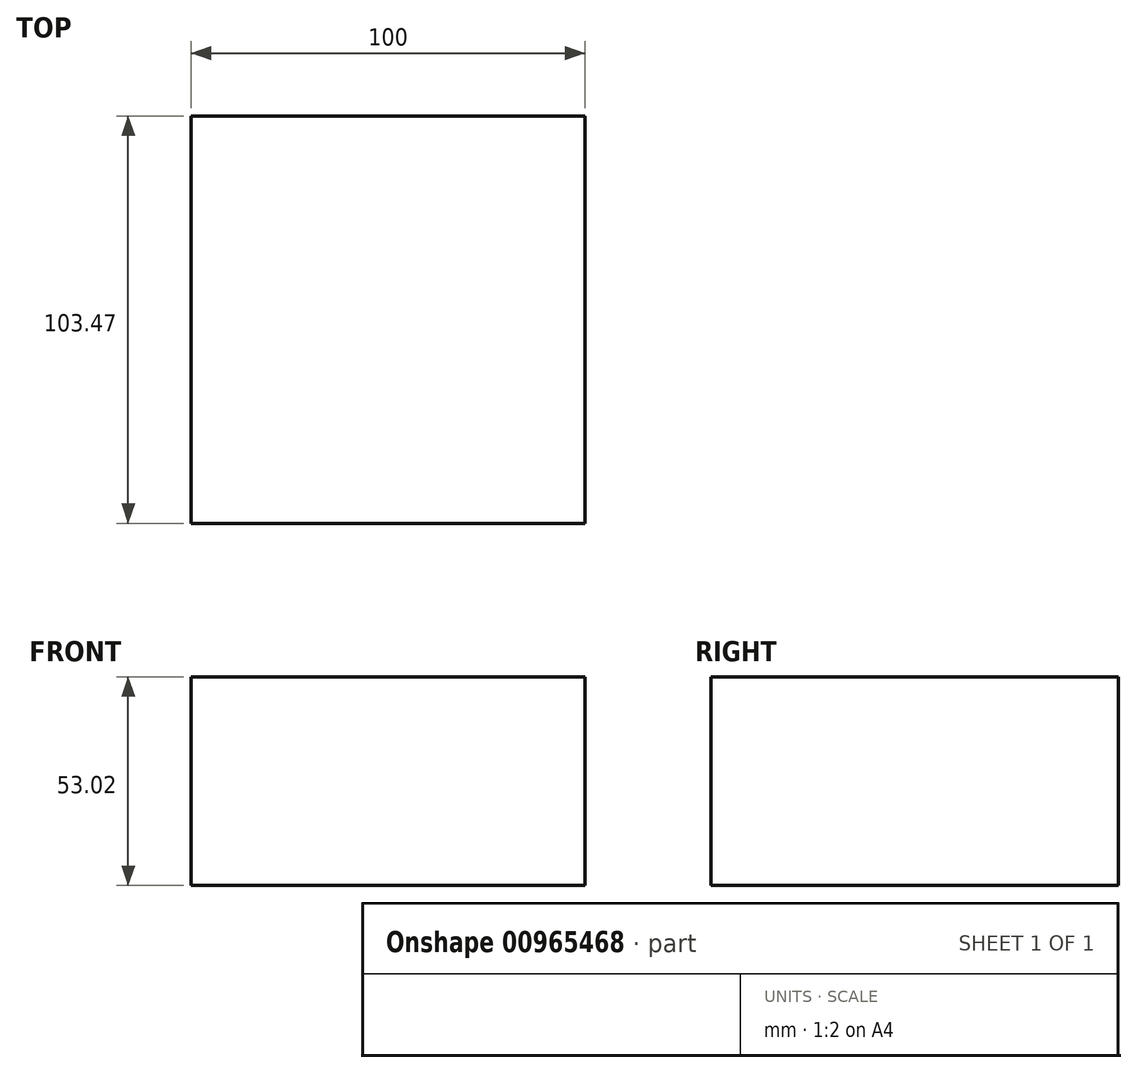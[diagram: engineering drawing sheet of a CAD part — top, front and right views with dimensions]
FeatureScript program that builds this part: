
annotation { "Feature Type Name" : "Feature", "Feature Type Description" : "" }
export const myFeature = defineFeature(function(context is Context, id is Id, definition is map)
    precondition{}
    {
        {
            var Q0;
            Q0=qCreatedBy(makeId("Right.planeOp"),FACE);
            var sketch = newSketch(context, id + "F0", { "sketchPlane" : qUnion([Q0])});
            skLineSegment(sketch, "E0.bottom", {"start": v(78.34, -33.2) * mm, "end": v(-25.13, -33.2) * mm});
            skLineSegment(sketch, "E0.top", {"start": v(78.34, 19.82) * mm, "end": v(-25.13, 19.82) * mm});
            skLineSegment(sketch, "E0.left", {"start": v(78.34, -33.2) * mm, "end": v(78.34, 19.82) * mm});
            skLineSegment(sketch, "E0.right", {"start": v(-25.13, -33.2) * mm, "end": v(-25.13, 19.82) * mm});
            skSolve(sketch);
        }
        {
            var Q0;
            Q0=makeQuery(id+"F0.imprint","IMPRINT",FACE,{"disambiguationData":[TD([[makeQuery(id+"F0.imprint","IMPRINT",EDGE,{"derivedFrom":sQuery(id+"F0.wireOp",EDGE,"E0.bottom")}),-1.0]])]});
            extrude(context, id + "F1", {"entities" : qUnion([Q0]), "depth" : 100 * mm, "offsetDistance" : 25.4 * mm});
        }
    });
